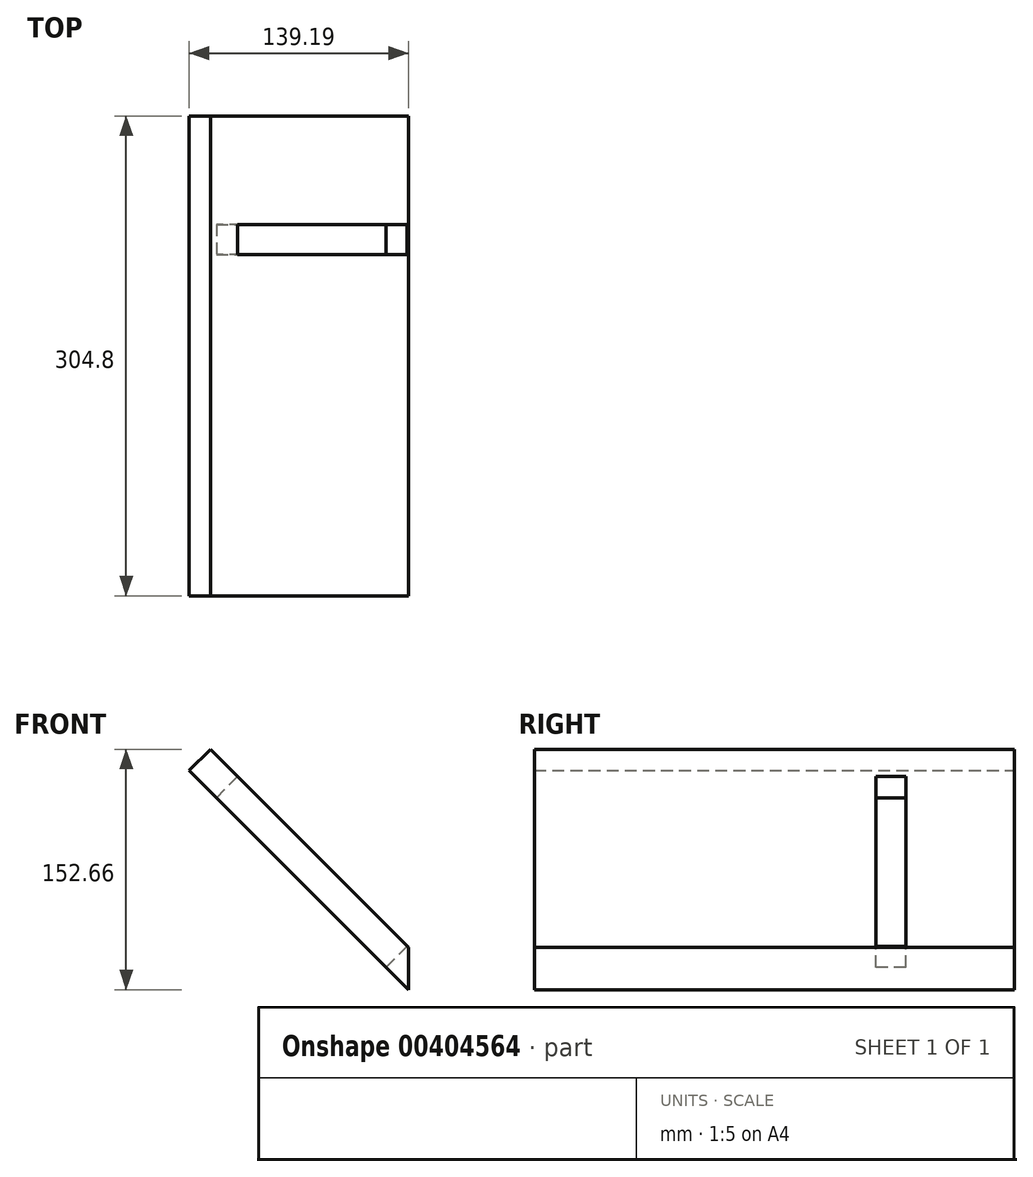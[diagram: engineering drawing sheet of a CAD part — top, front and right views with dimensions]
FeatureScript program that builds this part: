
annotation { "Feature Type Name" : "Feature", "Feature Type Description" : "" }
export const myFeature = defineFeature(function(context is Context, id is Id, definition is map)
    precondition{}
    {
        {
            var Q0;
            Q0=qCreatedBy(makeId("Front.planeOp"),FACE);
            var sketch = newSketch(context, id + "F0", { "sketchPlane" : qUnion([Q0])});
            skLineSegment(sketch, "E0.MirrorCS", {"start": v(378.53, 134.65) * mm, "end": v(239.34, 273.84) * mm});
            skLineSegment(sketch, "E1.MirrorCS", {"start": v(378.53, 161.6) * mm, "end": v(252.8, 287.31) * mm});
            skLineSegment(sketch, "E2.MirrorCS", {"start": v(378.53, 134.65) * mm, "end": v(378.53, 161.6) * mm});
            skLineSegment(sketch, "E3", {"start": v(252.8, 287.31) * mm, "end": v(239.34, 273.84) * mm});
            skSolve(sketch);
        }
        {
            var Q0;
            Q0=qSketchRegion(id+"F0",true);
            extrude(context, id + "F1", {"entities" : qUnion([Q0]), "endBound" : BoundingType.SYMMETRIC, "depth" : 304.8 * mm});
        }
        {
            var Q0;
            Q0=makeQuery(id+"F1.opExtrude","SWEPT_FACE",FACE,{"disambiguationData":[OSD([sQuery(id+"F0.wireOp",EDGE,"E1.MirrorCS")])]});
            var sketch = newSketch(context, id + "F2", { "sketchPlane" : qUnion([Q0])});
            skLineSegment(sketch, "E4.bottom", {"start": v(83.55, -152.4) * mm, "end": v(64.5, -152.4) * mm});
            skLineSegment(sketch, "E4.top", {"start": v(83.55, 0) * mm, "end": v(64.5, 0) * mm});
            skLineSegment(sketch, "E4.left", {"start": v(83.55, -152.4) * mm, "end": v(83.55, 0) * mm});
            skLineSegment(sketch, "E4.right", {"start": v(64.5, -152.4) * mm, "end": v(64.5, 0) * mm});
            skSolve(sketch);
        }
        {
            var Q0;
            Q0=qSketchRegion(id+"F2",true);
            extrude(context, id + "F3", {"entities" : qUnion([Q0]), "operationType" : NewBodyOperationType.REMOVE, "oppositeDirection" : true, "depth" : 19.05 * mm});
        }
    });
